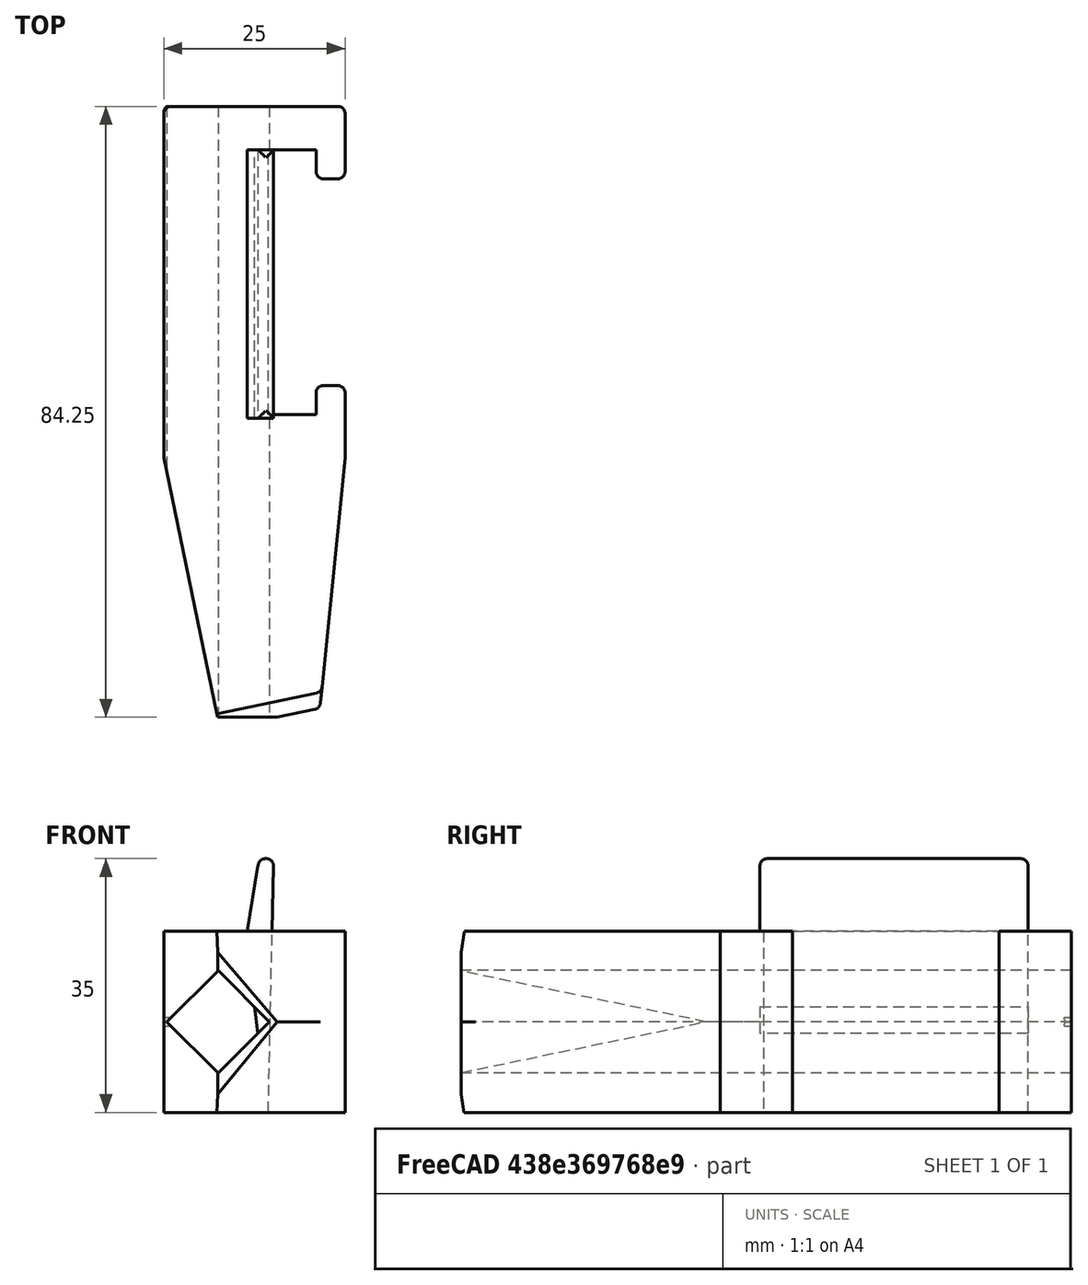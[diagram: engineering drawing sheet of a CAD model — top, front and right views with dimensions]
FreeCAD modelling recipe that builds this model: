
FCSTD DOCUMENT  (FreeCAD 0.19R)
Label: disher
License: All rights reserved
LicenseURL: http://en.wikipedia.org/wiki/All_rights_reserved
objects: Sketcher::SketchObject×5, PartDesign::Pad×2, PartDesign::Pocket×2, PartDesign::Fillet×2, PartDesign::Body×1, Mesh::Feature×1
note: 18 computed .brp shape members not serialized (recipe doc carries the construction recipe); baked Part::Feature solids carry a one-line shape summary decoded from their .brp

FEATURE [Sketcher::SketchObject] Sketch
  FullyConstrained = true
  MapMode = 5
  Support = -> [XY_Plane]
  sketch-geometry (14):
    g0: LineSegment StartX=0 StartY=-18.25 StartZ=0 EndX=0 EndY=18.25 EndZ=0
    g1: LineSegment StartX=0 StartY=18.25 StartZ=0 EndX=6.6 EndY=18.25 EndZ=0
    g2: LineSegment StartX=6.6 StartY=18.25 StartZ=0 EndX=6.6 EndY=14.25 EndZ=0
    g3: LineSegment StartX=6.6 StartY=14.25 StartZ=0 EndX=10.6 EndY=14.25 EndZ=0
    g4: LineSegment StartX=10.6 StartY=14.25 StartZ=0 EndX=10.6 EndY=24.25 EndZ=0
    g5: LineSegment StartX=10.6 StartY=24.25 StartZ=0 EndX=-14.4 EndY=24.25 EndZ=0
    g6: LineSegment StartX=-14.4 StartY=24.25 StartZ=0 EndX=-14.4 EndY=-24.25 EndZ=0
    g7: LineSegment StartX=10.6 StartY=-24.25 StartZ=0 EndX=10.6 EndY=-14.25 EndZ=0
    g8: LineSegment StartX=10.6 StartY=-14.25 StartZ=0 EndX=6.6 EndY=-14.25 EndZ=0
    g9: LineSegment StartX=6.6 StartY=-14.25 StartZ=0 EndX=6.6 EndY=-18.25 EndZ=0
    g10: LineSegment StartX=6.6 StartY=-18.25 StartZ=0 EndX=0 EndY=-18.25 EndZ=0
    g11: LineSegment StartX=-14.4 StartY=-24.25 StartZ=0 EndX=-7 EndY=-60 EndZ=0
    g12: LineSegment StartX=-7 StartY=-60 StartZ=0 EndX=7 EndY=-60 EndZ=0
    g13: LineSegment StartX=7 StartY=-60 StartZ=0 EndX=10.6 EndY=-24.25 EndZ=0
  constraints (37):
    c: PointOnObject(g0,g-2)
    c: Coincident(g0,g1)
    c: Horizontal(g1)
    c: Coincident(g1,g2)
    c: Coincident(g2,g3)
    c: Horizontal(g3)
    c: Coincident(g3,g4)
    c: Vertical(g4)
    c: Coincident(g4,g5)
    c: Coincident(g5,g6)
    c: Coincident(g7,g8)
    c: Coincident(g8,g9)
    c: Vertical(g9)
    c: Coincident(g9,g10)
    c: Coincident(g10,g0)
    c: Symmetric(g6,g5,g-1)
    c: Symmetric(g7,g4,g-1)
    c: Symmetric(g0,g0,g-1)
    c: Distance(g0) = 36.5
    c: Horizontal(g10)
    c: Equal(g10,g1)
    c: Distance(g1) = 6.6
    c: Vertical(g2)
    c: Horizontal(g8)
    c: Symmetric(g7,g3,g-1)
    c: Distance(g9) = 4
    c: Distance(g8) = 4
    c: Horizontal(g5)
    c: Distance(g7) = 10
    c: Distance(g5) = 25
    c: Coincident(g6,g11)
    c: Coincident(g11,g12)
    c: Coincident(g12,g13)
    c: Coincident(g13,g7)
    c: Symmetric(g12,g11,g-2)
    c: Distance(g12) = 14
    c: DistanceY(g12) = -60
FEATURE [PartDesign::Pad] Pad
  Direction = (1,1,1)
  Length = 25
  Length2 = 100
  Profile = -> Sketch
  Type = 0
FEATURE [Sketcher::SketchObject] Sketch001
  FullyConstrained = true
  MapMode = 5
  Placement = pos=(0,24.25,0) rot=(0,0.707107,0.707107;3.14159rad)
  Support = -> [Pad]
  sketch-geometry (4):
    g0: LineSegment StartX=6.92893 StartY=19.5711 StartZ=0 EndX=-0.142136 EndY=12.5 EndZ=0
    g1: LineSegment StartX=-0.142136 StartY=12.5 StartZ=0 EndX=6.92893 EndY=5.42893 EndZ=0
    g2: LineSegment StartX=6.92893 StartY=5.42893 StartZ=0 EndX=14 EndY=12.5 EndZ=0
    g3: LineSegment StartX=14 StartY=12.5 StartZ=0 EndX=6.92893 EndY=19.5711 EndZ=0
  constraints (12):
    c: Coincident(g0,g1)
    c: Coincident(g1,g2)
    c: Coincident(g2,g3)
    c: Coincident(g3,g0)
    c: Distance(g2) = 10
    c: Equal(g2,g3)
    c: Equal(g3,g0)
    c: Equal(g1,g0)
    c: Perpendicular(g0,g3)
    c: DistanceY(g2) = 12.5
    c: DistanceY(g0) = 12.5
    c: DistanceX(g2) = 14
FEATURE [PartDesign::Pocket] Pocket
  BaseFeature = -> Pad
  Length = 5
  Length2 = 100
  Profile = -> Sketch001
  Type = 1
FEATURE [Sketcher::SketchObject] Sketch002
  ExternalGeometry = -> [Pocket]
  FullyConstrained = false
  MapMode = 5
  Placement = pos=(0,18.25,0) rot=(1,0,0;1.5708rad)
  Support = -> [Pocket]
  sketch-geometry (4):
    g0: LineSegment StartX=0 StartY=-3.6e-15 StartZ=0 EndX=0.75 EndY=35 EndZ=0
    g1: LineSegment StartX=0.75 StartY=35 StartZ=0 EndX=-1.25 EndY=35 EndZ=0
    g2: LineSegment StartX=-1.25 StartY=35 StartZ=0 EndX=-3.13081 EndY=23.8315 EndZ=0
    g3: LineSegment StartX=-3.13081 StartY=23.8315 StartZ=0 EndX=0 EndY=-3.6e-15 EndZ=0
  constraints (9):
    c: Coincident(g-3,g0)
    c: Coincident(g0,g1)
    c: Horizontal(g1)
    c: Coincident(g1,g2)
    c: Coincident(g2,g3)
    c: Coincident(g3,g0)
    c: Distance(g1) = 2
    c: DistanceX(g-1,g0) = 0.75
    c: DistanceY(g0) = 35
FEATURE [PartDesign::Pad] Pad001
  BaseFeature = -> Pocket
  Direction = (1,1,1)
  Length = 37
  Length2 = 100
  Profile = -> Sketch002
  Type = 0
FEATURE [Sketcher::SketchObject] Sketch003
  FullyConstrained = false
  MapMode = 5
  Placement = pos=(-1.45e-14,18.25,-1.5e-15) rot=(0,0.707107,0.707107;3.14159rad)
  sketch-geometry (4):
    g0: LineSegment StartX=0 StartY=16.2446 StartZ=0 EndX=-4.24264 EndY=12.002 EndZ=0
    g1: LineSegment StartX=-4.24264 StartY=12.002 StartZ=0 EndX=0 EndY=7.75933 EndZ=0
    g2: LineSegment StartX=0 StartY=7.75933 StartZ=0 EndX=4.24264 EndY=12.002 EndZ=0
    g3: LineSegment StartX=4.24264 StartY=12.002 StartZ=0 EndX=0 EndY=16.2446 EndZ=0
  constraints (11):
    c: PointOnObject(g0,g-2)
    c: Coincident(g0,g1)
    c: PointOnObject(g1,g-2)
    c: Coincident(g1,g2)
    c: Coincident(g2,g3)
    c: Coincident(g3,g0)
    c: Equal(g0,g1)
    c: Equal(g1,g2)
    c: Equal(g2,g3)
    c: Perpendicular(g0,g3)
    c: Distance(g3) = 6
FEATURE [Sketcher::SketchObject] Sketch004
  FullyConstrained = false
  MapMode = 5
  Placement = pos=(-18.6217,-3.85456,0) rot=(0.655704,-0.533878,-0.533878;1.98084rad)
  Support = -> [Pad001]
  sketch-geometry (5):
    g0: LineSegment StartX=54 StartY=41.3236 StartZ=0 EndX=59 EndY=12.5 EndZ=0
    g1: LineSegment StartX=59 StartY=12.5 StartZ=0 EndX=54 EndY=-17.5224 EndZ=0
    g2: LineSegment StartX=54 StartY=-17.5224 StartZ=0 EndX=94.9088 EndY=-20.9534 EndZ=0
    g3: LineSegment StartX=94.9088 StartY=-20.9534 StartZ=0 EndX=94.9088 EndY=46.3218 EndZ=0
    g4: LineSegment StartX=94.9088 StartY=46.3218 StartZ=0 EndX=54 EndY=41.3236 EndZ=0
  constraints (10):
    c: Coincident(g0,g1)
    c: Coincident(g1,g2)
    c: Coincident(g2,g3)
    c: Vertical(g3)
    c: Coincident(g3,g4)
    c: Coincident(g4,g0)
    c: DistanceY(g0) = 12.5
    c: DistanceX(g0) = 54
    c: DistanceX(g1) = 54
    c: DistanceX(g0) = 59
FEATURE [PartDesign::Pocket] Pocket001
  BaseFeature = -> Pad001
  Length = 19
  Length2 = 100
  Profile = -> Sketch004
  Type = 0
FEATURE [PartDesign::Fillet] Fillet
  Base = -> Pocket001 [Edge40,Edge21,Edge46,Edge19,Edge48,Edge26,Edge27,Edge38]
  BaseFeature = -> Pocket001
  Radius = 1
  SupportTransform = false
FEATURE [PartDesign::Fillet] Fillet001
  Base = -> Fillet [Face25]
  BaseFeature = -> Fillet
  Radius = 1
  SupportTransform = false
FEATURE [PartDesign::Body] Body
  Group = -> [Sketch,Pad,Sketch001,Pocket,Sketch002,Pad001,Sketch003,Sketch004,Pocket001,Fillet,Fillet001]
  Origin = -> Origin
  Tip = -> Fillet001
FEATURE [Mesh::Feature] Mesh  label="Fillet001 (Meshed)"
